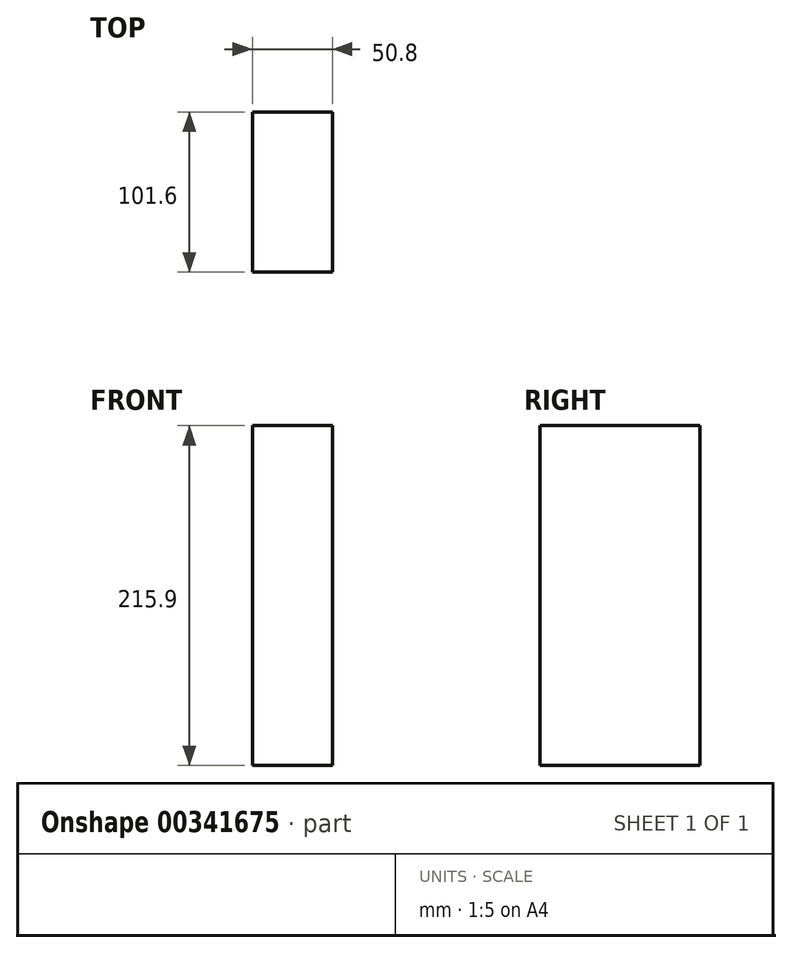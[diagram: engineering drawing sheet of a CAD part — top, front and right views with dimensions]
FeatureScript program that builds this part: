
annotation { "Feature Type Name" : "Feature", "Feature Type Description" : "" }
export const myFeature = defineFeature(function(context is Context, id is Id, definition is map)
    precondition{}
    {
        {
            var Q0;
            Q0=qCreatedBy(makeId("Front.planeOp"),FACE);
            var sketch = newSketch(context, id + "F0", { "sketchPlane" : qUnion([Q0])});
            skLineSegment(sketch, "E0.bottom", {"start": v(-86.05, 119.17) * mm, "end": v(-35.25, 119.17) * mm});
            skLineSegment(sketch, "E0.top", {"start": v(-86.05, -96.73) * mm, "end": v(-35.25, -96.73) * mm});
            skLineSegment(sketch, "E0.left", {"start": v(-86.05, 119.17) * mm, "end": v(-86.05, -96.73) * mm});
            skLineSegment(sketch, "E0.right", {"start": v(-35.25, 119.17) * mm, "end": v(-35.25, -96.73) * mm});
            skSolve(sketch);
        }
        {
            var Q0;
            Q0=makeQuery(id+"F0.imprint","IMPRINT",FACE,{"disambiguationData":[TD([[makeQuery(id+"F0.imprint","IMPRINT",EDGE,{"derivedFrom":sQuery(id+"F0.wireOp",EDGE,"E0.bottom")}),-1.0]])]});
            extrude(context, id + "F1", {"entities" : qUnion([Q0]), "depth" : 101.6 * mm, "offsetDistance" : 25.4 * mm});
        }
    });
